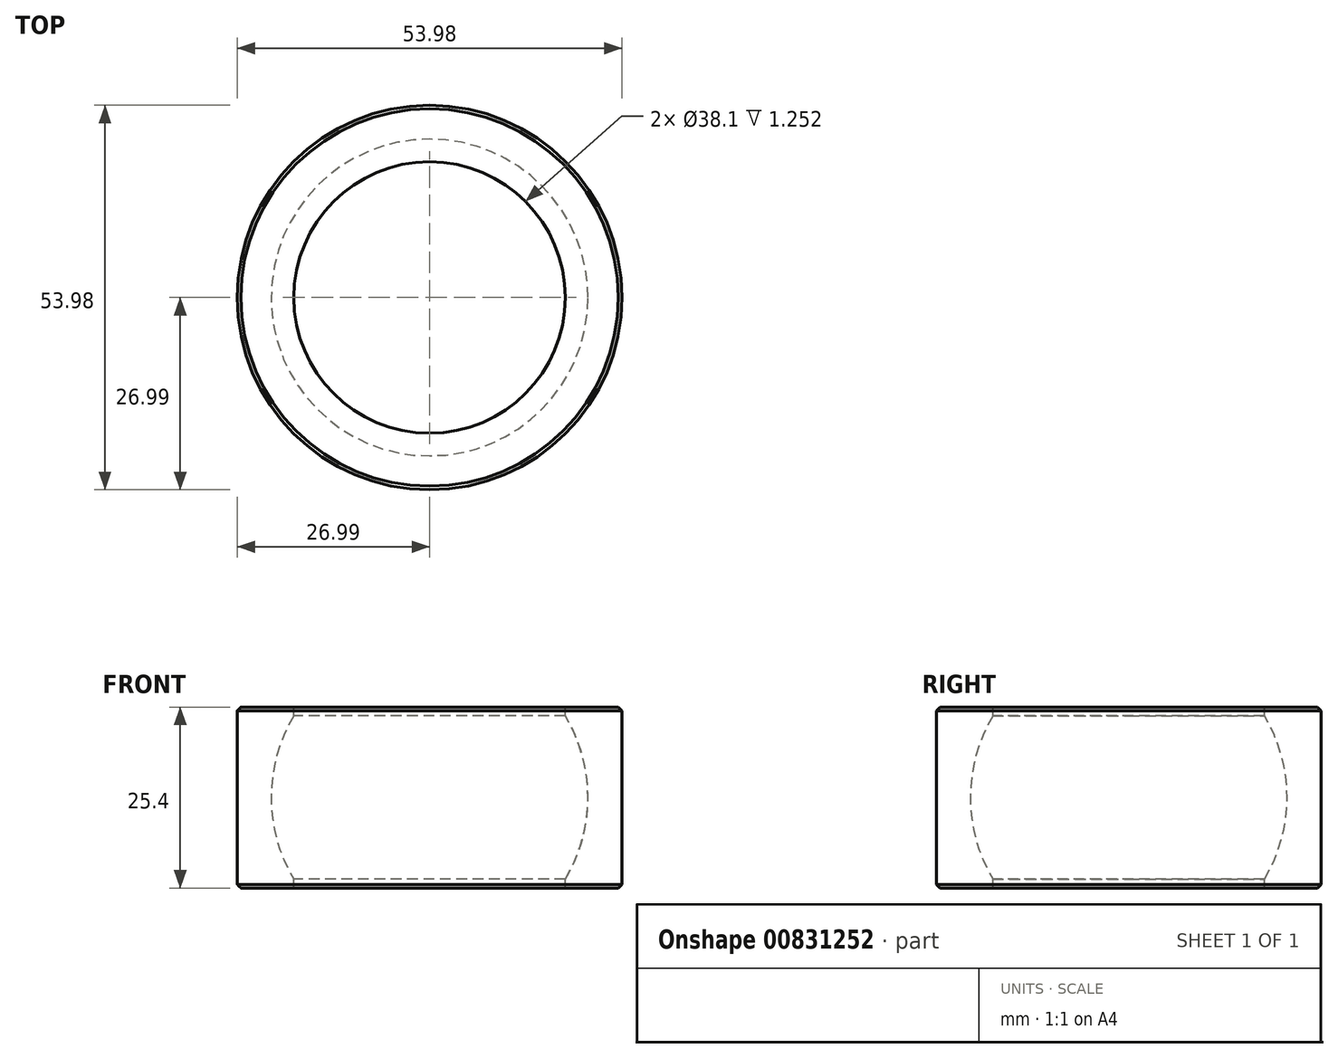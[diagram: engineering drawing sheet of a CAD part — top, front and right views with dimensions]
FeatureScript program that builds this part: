
annotation { "Feature Type Name" : "Feature", "Feature Type Description" : "" }
export const myFeature = defineFeature(function(context is Context, id is Id, definition is map)
    precondition{}
    {
        {
            var Q0;
            Q0=qCreatedBy(makeId("Front.planeOp"),FACE);
            var sketch = newSketch(context, id + "F0", { "sketchPlane" : qUnion([Q0])});
            skLineSegment(sketch, "E0", {"start": v(-26.99, -12.7) * mm, "end": v(-26.99, 12.7) * mm});
            skLineSegment(sketch, "E1", {"start": v(-26.99, 12.7) * mm, "end": v(-19.05, 12.7) * mm});
            skLineSegment(sketch, "E2", {"start": v(-19.05, 12.7) * mm, "end": v(-19.05, 11.45) * mm});
            skArc(sketch, "E3", {"start": v(-19.05, 11.45) * mm, "mid": v(-22.23, 0) * mm, "end": v(-19.05, -11.45) * mm});
            skLineSegment(sketch, "E4", {"start": v(-26.99, -12.7) * mm, "end": v(-19.05, -12.7) * mm});
            skLineSegment(sketch, "E5", {"start": v(-19.05, -12.7) * mm, "end": v(-19.05, -11.45) * mm});
            skLineSegment(sketch, "E6", {"start": v(0, 8.54) * mm, "end": v(0, -10.04) * mm, "construction": true});
            skSolve(sketch);
        }
        {
            var Q0;
            Q0 = qSketchRegion(id + "F0", true);
            var Q1;
            Q1=sQuery(id+"F0.wireOp",EDGE,"E6");
            revolve(context, id + "F1", {"surfaceOperationType" : NewSurfaceOperationType.NEW, "entities" : qUnion([Q0]), "axis" : qUnion([Q1]), "revolveType" : RevolveType.FULL});
        }
        {
            var Q0;
            Q0=makeQuery(id+"F1.opRevolve","SWEPT_EDGE",EDGE,{"disambiguationData":[OSD([sQuery(id+"F0.wireOp",EDGE,"E0"),sQuery(id+"F0.wireOp",EDGE,"E1")])]});
            var Q1;
            Q1=makeQuery(id+"F1.opRevolve","SWEPT_EDGE",EDGE,{"disambiguationData":[OSD([sQuery(id+"F0.wireOp",EDGE,"E0"),sQuery(id+"F0.wireOp",EDGE,"E4")])]});
            chamfer(context, id + "F2", {"entities" : qUnion([Q0, Q1]), "width" : 0.5 * mm, "tangentPropagation" : true});
        }
    });
